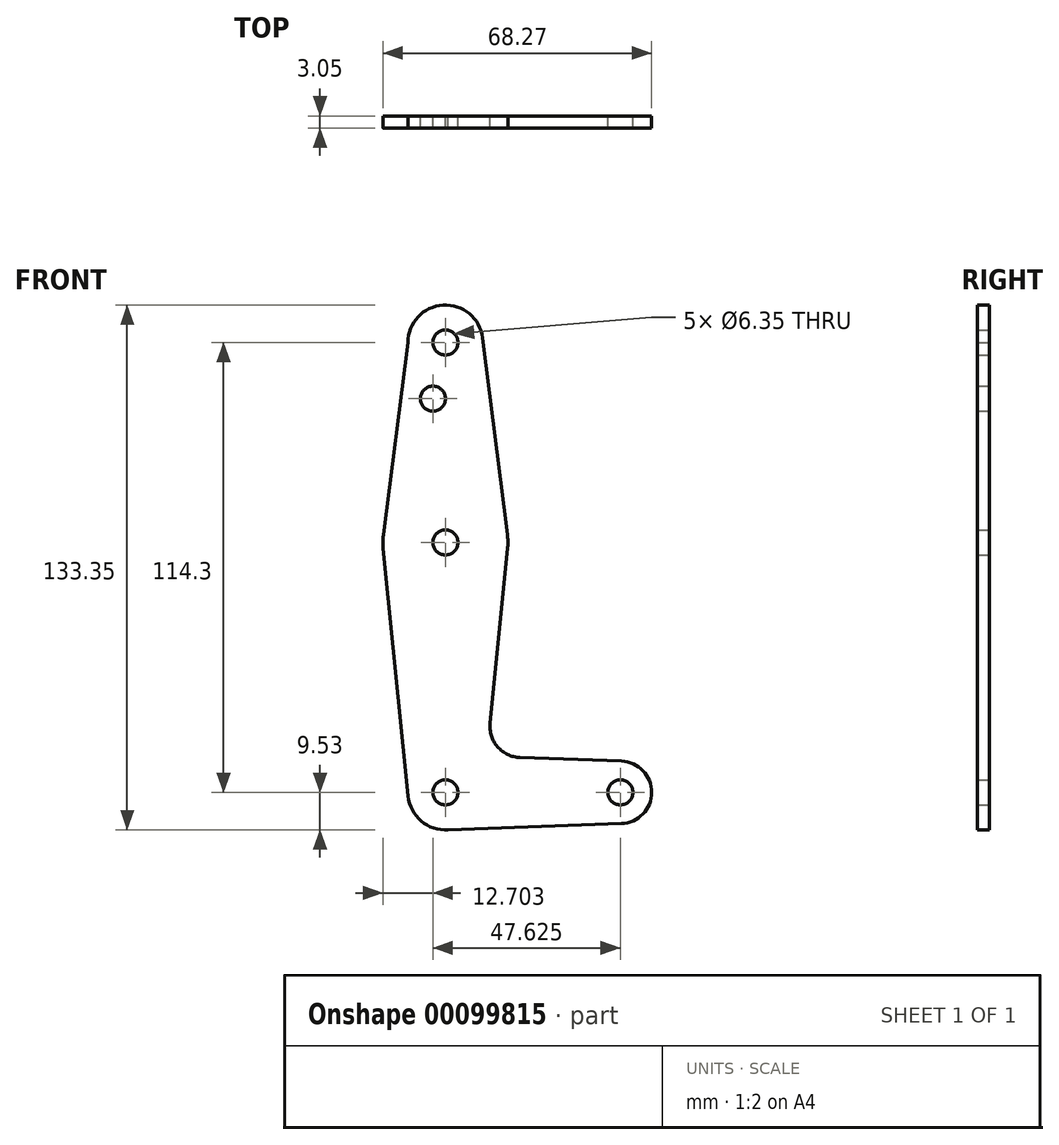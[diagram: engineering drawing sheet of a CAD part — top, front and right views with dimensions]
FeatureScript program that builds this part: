
annotation { "Feature Type Name" : "Feature", "Feature Type Description" : "" }
export const myFeature = defineFeature(function(context is Context, id is Id, definition is map)
    precondition{}
    {
        {
            var Q0;
            Q0=qCreatedBy(makeId("Front.planeOp"),FACE);
            var sketch = newSketch(context, id + "F0", { "sketchPlane" : qUnion([Q0])});
            skLineSegment(sketch, "E0", {"start": v(-31.47, 92.4) * mm, "end": v(-31.47, -21.9) * mm, "construction": true});
            skLineSegment(sketch, "E1", {"start": v(-31.47, -21.9) * mm, "end": v(12.98, -21.9) * mm, "construction": true});
            skCircle(sketch, "E2", {"center": v(-31.47, 92.4) * mm, "radius": 9.53 * mm});
            skCircle(sketch, "E3", {"center": v(-31.47, -21.9) * mm, "radius": 9.53 * mm});
            skCircle(sketch, "E4", {"center": v(12.98, -21.9) * mm, "radius": 7.94 * mm});
            skCircle(sketch, "E5", {"center": v(-31.47, 41.6) * mm, "radius": 15.88 * mm});
            skLineSegment(sketch, "E6", {"start": v(-41, 92.4) * mm, "end": v(-47.22, 43.62) * mm});
            skLineSegment(sketch, "E7", {"start": v(-47.27, 40.02) * mm, "end": v(-40.95, -22.84) * mm});
            skLineSegment(sketch, "E8", {"start": v(-22.02, 93.6) * mm, "end": v(-15.72, 43.6) * mm});
            skLineSegment(sketch, "E9", {"start": v(-15.68, 40.02) * mm, "end": v(-20.13, -4.3) * mm});
            skLineSegment(sketch, "E10", {"start": v(-12.5, -13.04) * mm, "end": v(13.26, -13.96) * mm});
            skLineSegment(sketch, "E11", {"start": v(-31.47, -31.42) * mm, "end": v(13.26, -29.82) * mm});
            skCircle(sketch, "E12", {"center": v(-34.65, 78.13) * mm, "radius": 3.17 * mm});
            skCircle(sketch, "E13", {"center": v(-31.47, 92.4) * mm, "radius": 3.17 * mm});
            skCircle(sketch, "E14", {"center": v(-31.47, 41.6) * mm, "radius": 3.17 * mm});
            skCircle(sketch, "E15", {"center": v(-31.47, -21.9) * mm, "radius": 3.18 * mm});
            skCircle(sketch, "E16", {"center": v(12.98, -21.9) * mm, "radius": 3.18 * mm});
            skPoint(sketch, "E17.newPointB", {"position": v(-31.47, -12.37) * mm});
            skArc(sketch, "E17.filletArc", {"start": v(-20.13, -4.3) * mm, "mid": v(-18.21, -10.32) * mm, "end": v(-12.5, -13.04) * mm});
            skSolve(sketch);
        }
        {
            var Q0;
            Q0 = qSketchRegion(id + "F0", true);
            extrude(context, id + "F1", {"entities" : qUnion([Q0]), "depth" : 3.05 * mm});
        }
    });
